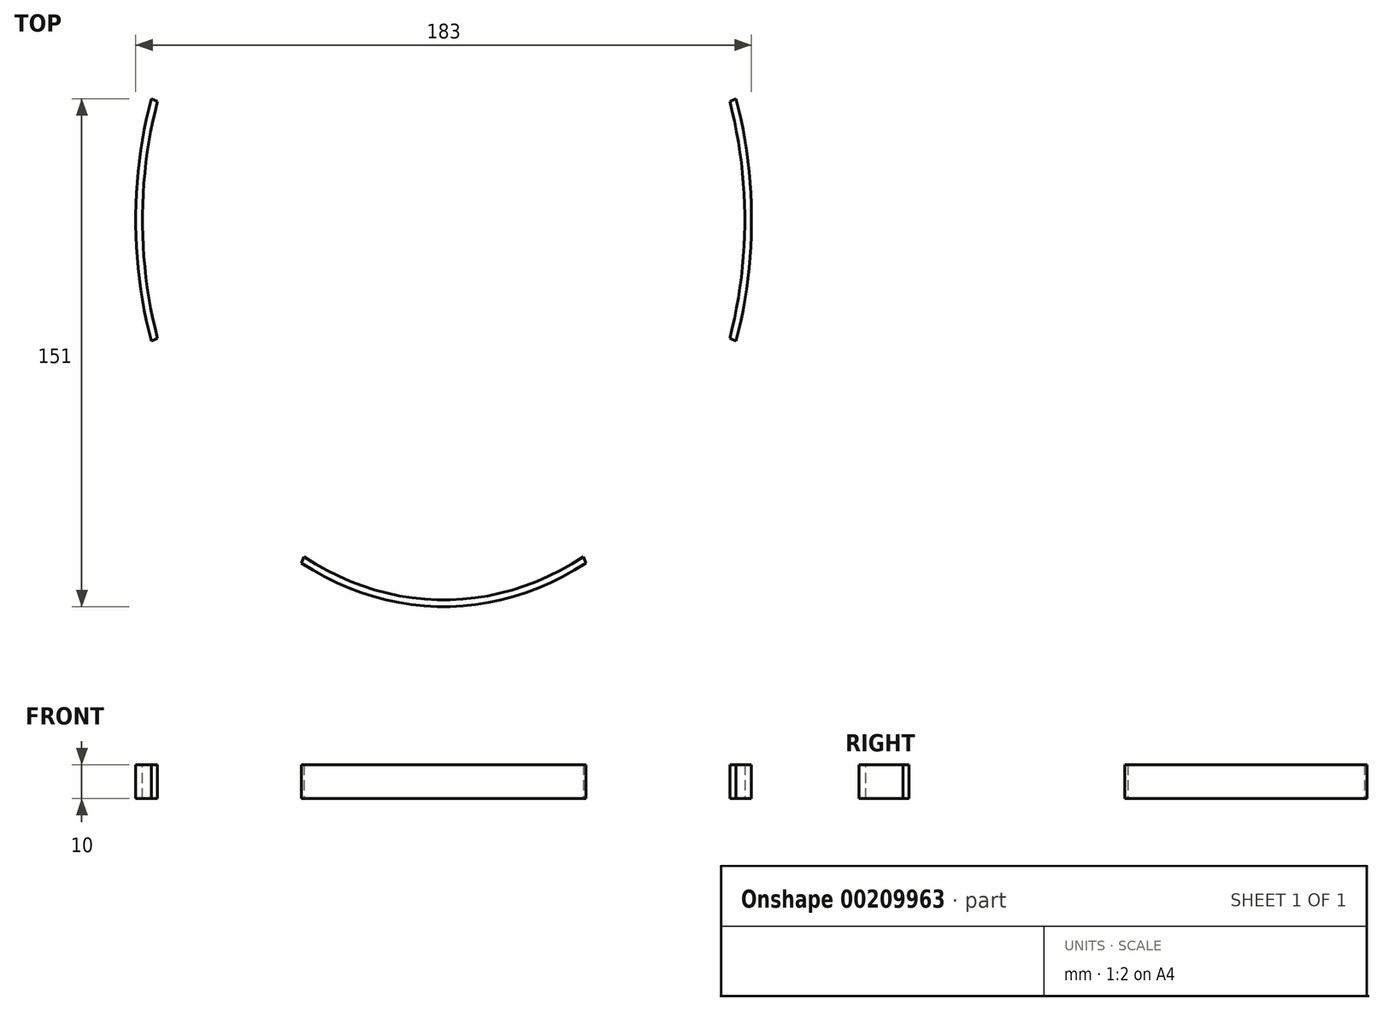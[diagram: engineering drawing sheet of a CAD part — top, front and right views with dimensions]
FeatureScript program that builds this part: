
annotation { "Feature Type Name" : "Feature", "Feature Type Description" : "" }
export const myFeature = defineFeature(function(context is Context, id is Id, definition is map)
    precondition{}
    {
        {
            var Q0;
            Q0=qCreatedBy(makeId("Top.planeOp"),FACE);
            var sketch = newSketch(context, id + "F0", { "sketchPlane" : qUnion([Q0])});
            skEllipse(sketch, "E0", {"center": v(0, 0) * mm, "majorRadius": 115 * mm, "minorRadius": 91.5 * mm, "majorAxis": v(0, 1)});
            skLineSegment(sketch, "E1", {"start": v(0, 0) * mm, "end": v(91.5, 0) * mm});
            skEllipse(sketch, "E2", {"center": v(0, 0) * mm, "majorRadius": 113 * mm, "minorRadius": 89.5 * mm, "majorAxis": v(0, 1)});
            skLineSegment(sketch, "E3", {"start": v(0, 0) * mm, "end": v(0, 113) * mm});
            skLineSegment(sketch, "E4", {"start": v(0, 113) * mm, "end": v(0, 115) * mm});
            skPoint(sketch, "E5", {"position": v(89.5, 0) * mm});
            skLineSegment(sketch, "E6", {"start": v(0, 0) * mm, "end": v(-89.5, 0) * mm});
            skLineSegment(sketch, "E7", {"start": v(-89.5, 0) * mm, "end": v(-91.5, 0) * mm});
            skLineSegment(sketch, "E8", {"start": v(-86.9, 36) * mm, "end": v(0, 0) * mm});
            skLineSegment(sketch, "E9", {"start": v(0, 0) * mm, "end": v(-86.9, -36) * mm});
            skPoint(sketch, "E10", {"position": v(-85.04, 35.22) * mm});
            skPoint(sketch, "E11", {"position": v(-85.04, -35.22) * mm});
            skPoint(sketch, "E12", {"position": v(-42.25, -102) * mm});
            skPoint(sketch, "E13", {"position": v(41.48, -100.13) * mm});
            skPoint(sketch, "E14", {"position": v(42.25, -102) * mm});
            skPoint(sketch, "E15", {"position": v(-41.48, -100.13) * mm});
            skLineSegment(sketch, "E16", {"start": v(-42.25, -102) * mm, "end": v(0, 0) * mm});
            skLineSegment(sketch, "E17", {"start": v(42.25, -102) * mm, "end": v(0, 0) * mm});
            skSolve(sketch);
        }
        {
            var Q0;
            {var subQ0=sQuery(id+"F0.wireOp",EDGE,"E7");Q0=makeQuery(id+"F0.imprint","IMPRINT",FACE,{"disambiguationData":[TD([[makeQuery(id+"F0.imprint","IMPRINT",EDGE,{"derivedFrom":subQ0}),-1.0]])]});}
            var Q1;
            {var subQ0=sQuery(id+"F0.wireOp",EDGE,"E7");Q1=makeQuery(id+"F0.imprint","IMPRINT",FACE,{"disambiguationData":[TD([[makeQuery(id+"F0.imprint","IMPRINT",EDGE,{"derivedFrom":subQ0}),1.0]])]});}
            extrude(context, id + "F1", {"entities" : qUnion([Q0, Q1]), "depth" : 10 * mm});
        }
        {
            var Q0;
            Q0=makeQuery(id+"F1.opExtrude","SWEPT_BODY",BODY,{"disambiguationData":[OSD([sQuery(id+"F0.wireOp",EDGE,"E0"),sQuery(id+"F0.wireOp",EDGE,"E2"),sQuery(id+"F0.wireOp",EDGE,"E8"),sQuery(id+"F0.wireOp",EDGE,"E9")])]});
            var Q1;
            Q1=qCreatedBy(makeId("Right.planeOp"),FACE);
            mirror(context, id + "F2", {"entities" : qUnion([Q0]), "mirrorPlane" : qUnion([Q1])});
        }
        {
            var Q0;
            {var subQ0=sQuery(id+"F0.wireOp",EDGE,"E16");var subQ1=sQuery(id+"F0.wireOp",EDGE,"E0");var subQ2=makeQuery(id+"F0.imprint","INTERSECT",VERTEX,{"derivedFrom":[subQ1,subQ0]});Q0=makeQuery(id+"F0.imprint","IMPRINT",FACE,{"disambiguationData":[TD([[makeQuery(id+"F0.imprint","IMPRINT",EDGE,{"disambiguationData":[TD([[subQ2,-1.0]])],"derivedFrom":subQ1}),1.0]])]});}
            extrude(context, id + "F3", {"entities" : qUnion([Q0]), "depth" : 10 * mm});
        }
    });
